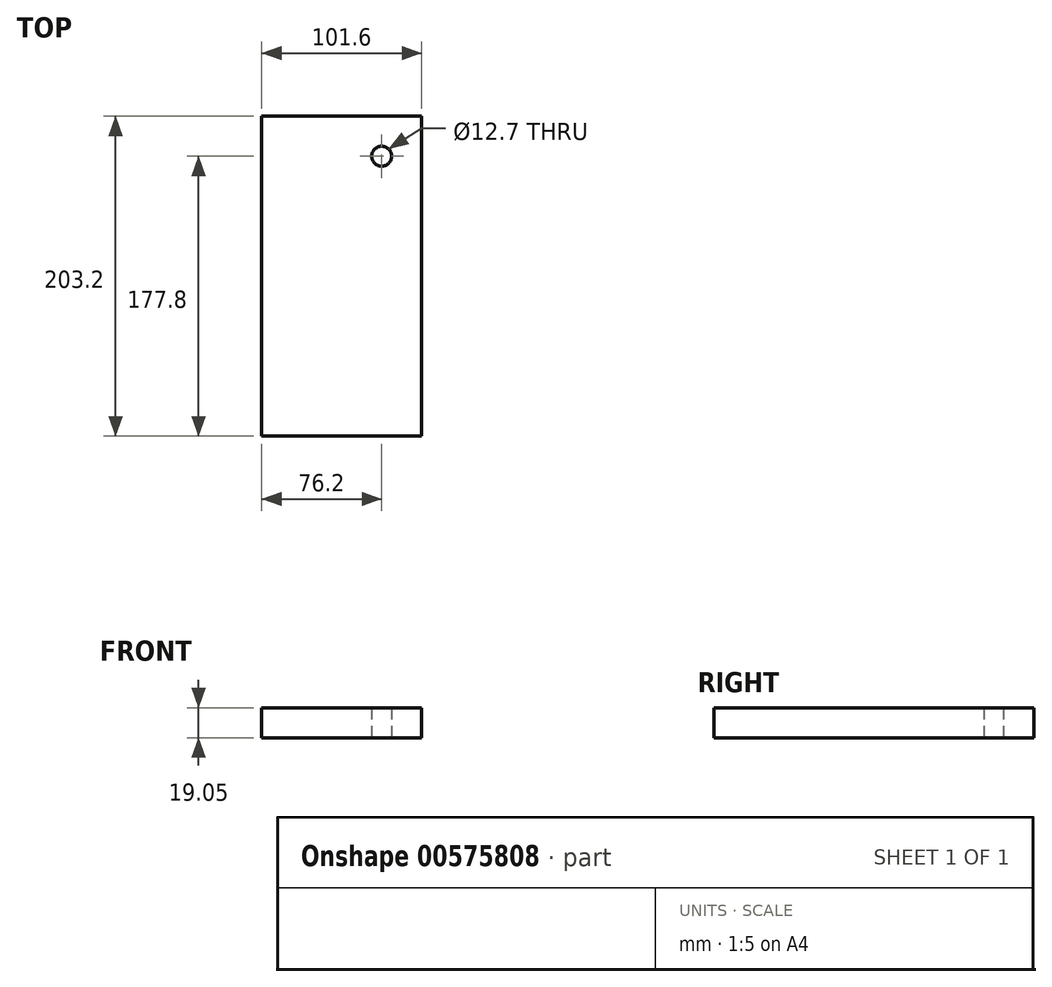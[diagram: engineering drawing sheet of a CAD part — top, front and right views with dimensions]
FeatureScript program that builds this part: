
annotation { "Feature Type Name" : "Feature", "Feature Type Description" : "" }
export const myFeature = defineFeature(function(context is Context, id is Id, definition is map)
    precondition{}
    {
        {
            var Q0;
            Q0=qCreatedBy(makeId("Top.planeOp"),FACE);
            var sketch = newSketch(context, id + "F0", { "sketchPlane" : qUnion([Q0])});
            skLineSegment(sketch, "E0.bottom", {"start": v(50.8, 101.6) * mm, "end": v(-50.8, 101.6) * mm});
            skLineSegment(sketch, "E0.top", {"start": v(50.8, -101.6) * mm, "end": v(-50.8, -101.6) * mm});
            skLineSegment(sketch, "E0.left", {"start": v(50.8, 101.6) * mm, "end": v(50.8, -101.6) * mm});
            skLineSegment(sketch, "E0.right", {"start": v(-50.8, 101.6) * mm, "end": v(-50.8, -101.6) * mm});
            skPoint(sketch, "E0.middle", {"position": v(0, 0) * mm});
            skCircle(sketch, "E1", {"center": v(25.4, 76.2) * mm, "radius": 6.35 * mm});
            skSolve(sketch);
        }
        {
            var Q0;
            Q0=makeQuery(id+"F0.imprint","IMPRINT",FACE,{"disambiguationData":[TD([[makeQuery(id+"F0.imprint","IMPRINT",EDGE,{"derivedFrom":sQuery(id+"F0.wireOp",EDGE,"E0.bottom")}),1.0]])]});
            extrude(context, id + "F1", {"entities" : qUnion([Q0]), "depth" : 19.05 * mm, "offsetDistance" : 25.4 * mm});
        }
    });
